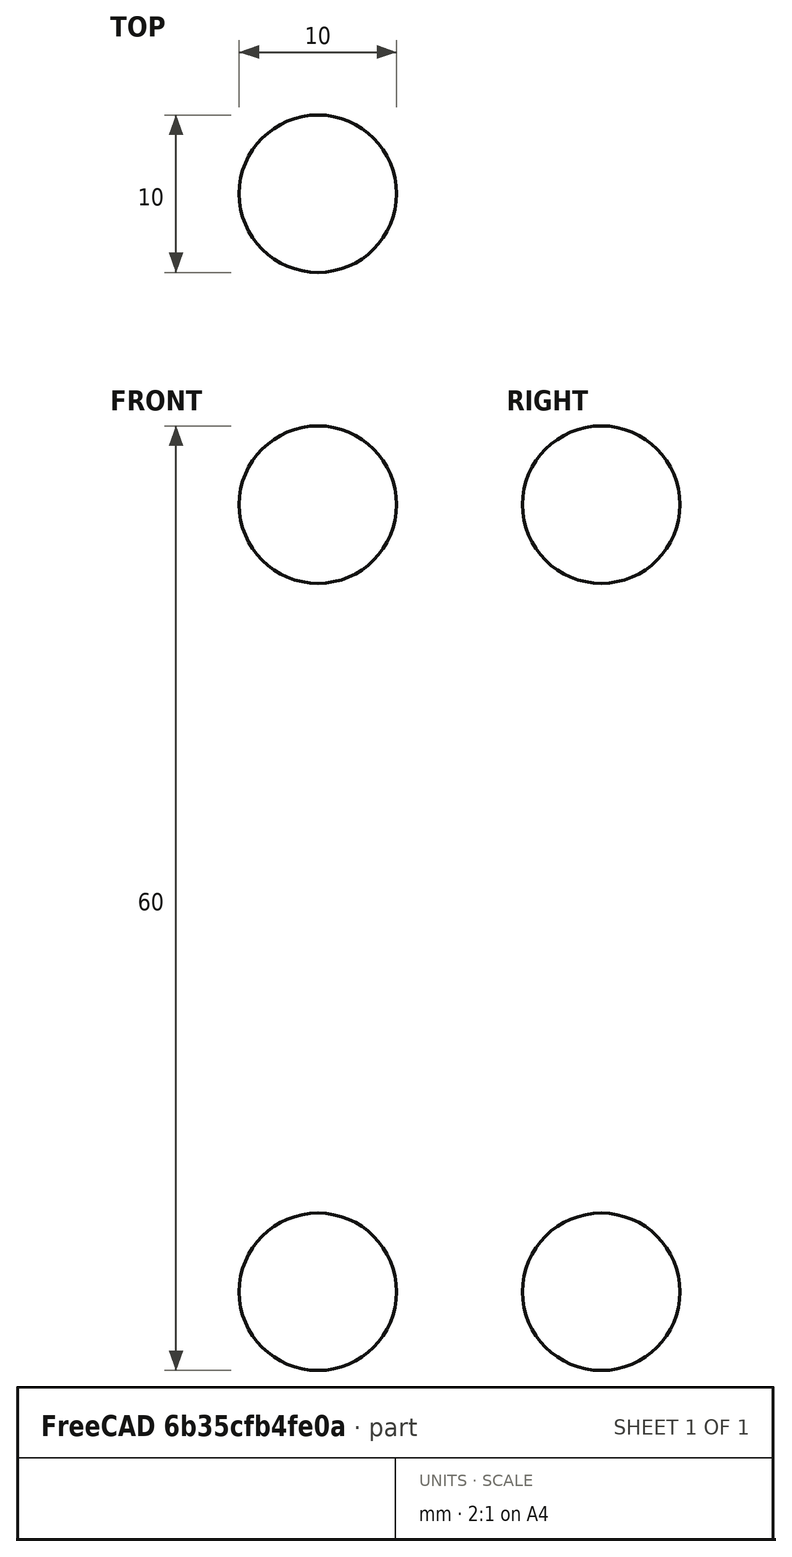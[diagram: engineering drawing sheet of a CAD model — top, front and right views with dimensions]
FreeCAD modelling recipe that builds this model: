
FCSTD DOCUMENT  (FreeCAD 0.22R35966 (Git))
Label: MassSpringDamper
License: All rights reserved
LicenseURL: http://en.wikipedia.org/wiki/All_rights_reserved
objects: App::DocumentObjectGroupPython×56, PartDesign::CoordinateSystem×6, App::TextDocument×3, Part::Line×3, App::Part×3, App::FeaturePython×2, Part::Sphere×2, Part::FeaturePython×2, App::DocumentObjectGroup×1, App::MaterialObjectPython×1
note: 13 computed .brp shape members not serialized (recipe doc carries the construction recipe); baked Part::Feature solids carry a one-line shape summary decoded from their .brp

FEATURE [App::DocumentObjectGroupPython] MBD_animated_vectors  # scripted group (container) (typed FeaturePython)
FEATURE [App::DocumentObjectGroupPython] MBD_constitutive_laws  # scripted group (container) (typed FeaturePython)
FEATURE [App::DocumentObjectGroupPython] MBD_drives_and_drive_callers  # scripted group (container) (typed FeaturePython)
FEATURE [App::DocumentObjectGroupPython] MBD_abstract_nodes  # scripted group (container) (typed FeaturePython)
FEATURE [App::DocumentObjectGroupPython] MBD_dummy_nodes  # scripted group (container) (typed FeaturePython)
FEATURE [App::DocumentObjectGroupPython] MBD_hydraulic_nodes  # scripted group (container) (typed FeaturePython)
FEATURE [App::DocumentObjectGroupPython] MBD_beam_elements  # scripted group (container) (typed FeaturePython)
FEATURE [App::DocumentObjectGroupPython] MBD_genel_clamps  # scripted group (container) (typed FeaturePython)
FEATURE [App::DocumentObjectGroupPython] MBD_genel_elements  # scripted group (container) (typed FeaturePython)
  Group = -> [MBD_genel_clamps]
FEATURE [App::DocumentObjectGroupPython] MBD_gravity_elements  # scripted group (container) (typed FeaturePython)
FEATURE [App::DocumentObjectGroupPython] MBD_hydraulic_fluid_elements  # scripted group (container) (typed FeaturePython)
FEATURE [App::DocumentObjectGroupPython] MBD_hydraulic_elements  # scripted group (container) (typed FeaturePython)
  Group = -> [MBD_hydraulic_fluid_elements]
FEATURE [App::DocumentObjectGroupPython] MBD_angular_acceleration_joints  # scripted group (container) (typed FeaturePython)
FEATURE [App::DocumentObjectGroupPython] MBD_angular_velocity_joints  # scripted group (container) (typed FeaturePython)
FEATURE [App::DocumentObjectGroupPython] MBD_assembly_joints  # scripted group (container) (typed FeaturePython)
FEATURE [App::DocumentObjectGroupPython] MBD_coincidence_joints  # scripted group (container) (typed FeaturePython)
FEATURE [App::DocumentObjectGroupPython] MBD_cylindrical_joints  # scripted group (container) (typed FeaturePython)
FEATURE [App::DocumentObjectGroupPython] MBD_deformable_axial_joints  # scripted group (container) (typed FeaturePython)
FEATURE [App::DocumentObjectGroupPython] MBD_deformable_displacement_joints  # scripted group (container) (typed FeaturePython)
FEATURE [App::DocumentObjectGroupPython] MBD_deformable_hinge_joints  # scripted group (container) (typed FeaturePython)
FEATURE [App::DocumentObjectGroupPython] MBD_distance_joints  # scripted group (container) (typed FeaturePython)
FEATURE [App::DocumentObjectGroupPython] MBD_drive_hinge_joints  # scripted group (container) (typed FeaturePython)
FEATURE [App::DocumentObjectGroupPython] MBD_in_line_joints  # scripted group (container) (typed FeaturePython)
FEATURE [App::DocumentObjectGroupPython] MBD_in_plane_joints  # scripted group (container) (typed FeaturePython)
FEATURE [App::DocumentObjectGroupPython] MBD_linear_acceleration_joints  # scripted group (container) (typed FeaturePython)
FEATURE [App::DocumentObjectGroupPython] MBD_linear_velocity_joints  # scripted group (container) (typed FeaturePython)
FEATURE [App::DocumentObjectGroupPython] MBD_prismatic_joints  # scripted group (container) (typed FeaturePython)
FEATURE [App::DocumentObjectGroupPython] MBD_hinge_joints  # scripted group (container) (typed FeaturePython)
FEATURE [App::DocumentObjectGroupPython] MBD_revolute_pin_joints  # scripted group (container) (typed FeaturePython)
FEATURE [App::DocumentObjectGroupPython] MBD_revolute_rotation_joints  # scripted group (container) (typed FeaturePython)
FEATURE [App::DocumentObjectGroupPython] MBD_shock_absorber_joints  # scripted group (container) (typed FeaturePython)
FEATURE [App::DocumentObjectGroupPython] MBD_slider_joints  # scripted group (container) (typed FeaturePython)
FEATURE [App::DocumentObjectGroupPython] MBD_spherical_hinge_joints  # scripted group (container) (typed FeaturePython)
FEATURE [App::DocumentObjectGroupPython] MBD_total_joints  # scripted group (container) (typed FeaturePython)
FEATURE [App::DocumentObjectGroupPython] MBD_total_pin_joints  # scripted group (container) (typed FeaturePython)
FEATURE [App::DocumentObjectGroupPython] MBD_viscous_body_joints  # scripted group (container) (typed FeaturePython)
FEATURE [App::DocumentObjectGroupPython] MBD_dummy_body_elements  # scripted group (container) (typed FeaturePython)
FEATURE [App::DocumentObjectGroupPython] MBD_gear_body_elements  # scripted group (container) (typed FeaturePython)
FEATURE [App::DocumentObjectGroupPython] MBD_structural_couple_elements  # scripted group (container) (typed FeaturePython)
FEATURE [App::DocumentObjectGroupPython] MBD_scalar_functions  # scripted group (container) (typed FeaturePython)
FEATURE [App::TextDocument] ELEMENT_input_file
  Text = <blob: 7349 chars omitted>
FEATURE [App::TextDocument] ELEMENT_input_file_aux
FEATURE [App::DocumentObjectGroupPython] MBD_input_files  # scripted group (container) (typed FeaturePython)
  Group = -> [ELEMENT_input_file,ELEMENT_input_file_aux]
FEATURE [App::TextDocument] ELEMENT_variables
  Text = K = 1; #Spring constant\nC = 0.01; #Damping constant
FEATURE [App::DocumentObjectGroupPython] MBD_user_defined_variables  # scripted group (container) (typed FeaturePython)
  Group = -> [ELEMENT_variables]
FEATURE [Part::Line] ELEMENT_cmx
  AttacherType = Attacher::AttachEngine3D
  X1 = -1e-16
  X2 = -1e-16
  Y1 = -1e-16
  Y2 = -1e-16
  Z1 = 2e-16
  Z2 = 50
FEATURE [Part::Line] ELEMENT_cmy
  AttacherType = Attacher::AttachEngine3D
  X1 = 0
  X2 = 0
  Y1 = 0
  Y2 = 0
  Z1 = 0
  Z2 = 1
FEATURE [Part::Line] ELEMENT_cmz
  AttacherType = Attacher::AttachEngine3D
  X1 = 0
  X2 = 0
  Y1 = 0
  Y2 = 0
  Z1 = 0
  Z2 = 1
FEATURE [PartDesign::CoordinateSystem] ELEMENT_ground
  AttacherType = Attacher::AttachEngine3D
FEATURE [App::DocumentObjectGroupPython] MBD_global_reference_frame  # scripted group (container) (typed FeaturePython)
  Group = -> [ELEMENT_cmx,ELEMENT_cmy,ELEMENT_cmz,ELEMENT_ground]
FEATURE [App::FeaturePython] ELEMENT_parameters  # WARN: FeaturePython — macro-defined, semantics opaque (R4)
  assembly_max_iterations = 1000
  default_orientation = 0
  derivatives_coefficient = auto
  derivatives_max_iterations = 100
  derivatives_tolerance = 0.0001
  final_time = 10
  initial_position_stiffness = 1
  initial_time = 0
  initial_velocity_stiffness = 1
  integration_max_iterations = 100
  model = 0
  modules_to_load = 0
  omega_rotates = 0
  output_data = 0
  output_meter = 1
  path_to_ELEMENT_executable = <userpath>/.local/share/FreeCAD/Mod/FreeCAD-motion-workbench-master/mbdyn-1.7.3-executables/LinuxExecutable/mbdyn
  print = 0
  skip_initial_joint_assembly = 0
  solver = 0
  time_step = 0.01
  tolerance = 1e-06
  type_of_path_to_ELEMENT_executable = 0
  type_of_path_to_run_time_loadable_modules = 0
  type_of_working_directory = 0
  units = 0
FEATURE [App::FeaturePython] ELEMENT_animation  # WARN: FeaturePython — macro-defined, semantics opaque (R4)
  animationClicked = false
  assembled = true
  association0 = none
  association1 = none
  association2 = none
  association3 = none
  association4 = none
  association5 = none
  association6 = none
  association7 = none
  association8 = none
  association9 = none
  bodies_line_width = 1
  bodies_point_size = 4
  characteristic_length = 100
  continous = true
  current_time = 0
  current_time_step = 0
  follow_selected_object = false
  highlight_element = true
  objects_to_animate = 0
  speed = 10
  stop_at_time = 0
  stop_at_time_step = 0
  subAssembly = true
  transparency_when_assembled = 0
  transparency_when_exploded = 50
  zoon_when_contracted = 0.5
  zoon_when_expanded = 1
FEATURE [App::DocumentObjectGroupPython] MBD_simulation_parameters  # scripted group (container) (typed FeaturePython)
  Group = -> [ELEMENT_parameters,ELEMENT_animation]
FEATURE [Part::Sphere] Sphere
  Angle1 = -90
  Angle2 = 90
  Angle3 = 360
  AttacherType = Attacher::AttachEngine3D
  Radius = 5
FEATURE [App::Part] Part  label="Grounded node"
  Group = -> [Sphere]
  Origin = -> Origin001
FEATURE [Part::Sphere] Sphere001
  Angle1 = -90
  Angle2 = 90
  Angle3 = 360
  AttacherType = Attacher::AttachEngine3D
  Radius = 5
FEATURE [App::Part] Part001  label="Oscillating mass"
  Group = -> [Sphere001]
  Origin = -> Origin002
  Placement = pos=(0,0,50) rot=(0,0,1;0rad)
FEATURE [App::DocumentObjectGroup] Group  label="CAD"
  Group = -> [Part,Part001]
FEATURE [Part::FeaturePython] ELEMENT_static_body_1  # WARN: FeaturePython — macro-defined, semantics opaque (R4)
  absolute_center_of_mass_X = 0
  absolute_center_of_mass_Y = -1e-16
  absolute_center_of_mass_Z = -1e-16
  base_entity = Part
  label = 1
  type = static
FEATURE [App::DocumentObjectGroupPython] MBD_static_body_elements  # scripted group (container) (typed FeaturePython)
  Group = -> [ELEMENT_static_body_1]
FEATURE [PartDesign::CoordinateSystem] ELEMENT_structural_static_1
  AttacherType = Attacher::AttachEngine3D
  Placement = pos=(0,-1e-16,-1e-16) rot=(0,0,1;0rad)
  absolute_angular_velocity_X = 0
  absolute_angular_velocity_Y = 0
  absolute_angular_velocity_Z = 0
  absolute_orientation_matrix = 3, 0.0, 0.0, 1.0, 2, 0.0, 1.0, 0.0
  absolute_position_X = 0
  absolute_position_Y = -1e-16
  absolute_position_Z = -1e-16
  absolute_velocity_X = 0
  absolute_velocity_Y = 0
  absolute_velocity_Z = 0
  base_entity = -> ELEMENT_static_body_1
  initial_conditions_reference_system_angular_velocity = 0
  initial_conditions_reference_system_velocity = 0
  label = 1
  offset_pitch = 0
  offset_reference_system_orientation = 0
  offset_reference_system_position = 0
  offset_roll = 0
  offset_x = 0
  offset_y = 0
  offset_yaw = 0
  offset_z = 0
  placement_method = 0
  plugin_variables = none
  type = static
FEATURE [App::DocumentObjectGroupPython] MBD_structural_static_nodes  # scripted group (container) (typed FeaturePython)
  Group = -> [ELEMENT_structural_static_1]
FEATURE [PartDesign::CoordinateSystem] ELEMENT_clamp_joint_1
  AttacherType = Attacher::AttachEngine3D
  Placement = pos=(0,-1e-16,-1e-16) rot=(0,0,1;0rad)
  absolute_orientation_matrix = 3, 0.0, 0.0, 1.0, 2, 0.0, 1.0, 0.0
  absolute_pin_position_X = 0
  absolute_pin_position_Y = -1e-16
  absolute_pin_position_Z = -1e-16
  assembly_joint = false
  base_entity = -> ELEMENT_static_body_1
  driven_element = false
  driven_element_expression = Time <= 1.0
  group = 0
  joint = clamp
  joint_activation = 0
  label = 1
  plugin_variables = none
FEATURE [App::DocumentObjectGroupPython] MBD_clamp_joints  # scripted group (container) (typed FeaturePython)
  Group = -> [ELEMENT_clamp_joint_1]
FEATURE [App::DocumentObjectGroupPython] MBD_joint_elements  # scripted group (container) (typed FeaturePython)
  Group = -> [MBD_angular_acceleration_joints,MBD_angular_velocity_joints,MBD_assembly_joints,MBD_clamp_joints,MBD_coincidence_joints,MBD_cylindrical_joints,MBD_deformable_axial_joints,MBD_deformable_displacement_joints,MBD_deformable_hinge_joints,MBD_distance_joints,MBD_drive_hinge_joints,MBD_in_line_joints,MBD_in_plane_joints,MBD_linear_acceleration_joints,MBD_linear_velocity_joints,MBD_prismatic_joints,+9 more]
FEATURE [Part::FeaturePython] ELEMENT_rigid_body_2  # WARN: FeaturePython — macro-defined, semantics opaque (R4)
  FirstAxisOfInertia = (0,0,1)
  Ixx = 0.0413643
  Iyy = 0.0413643
  Izz = 0.0413643
  SecondAxisOfInertia = (0,-1,0)
  ThirdAxisOfInertia = (1,0,0)
  absolute_center_of_mass_X = 0
  absolute_center_of_mass_Y = -1e-16
  absolute_center_of_mass_Z = 50
  base_entity = Part001
  density = 7.9e-06
  ixx = 5235.99
  iyy = 5235.99
  izz = 5235.99
  label = 2
  mass = 0.00413643
  material = Steel-Generic
  material_definition = 0
  material_object = ELEMENT_material_2
  node = 2
  relative_center_of_mass_X = 0
  relative_center_of_mass_Y = 0
  relative_center_of_mass_Z = 0
  type = rigid
  volume = 523.599
FEATURE [App::DocumentObjectGroupPython] MBD_rigid_body_elements  # scripted group (container) (typed FeaturePython)
  Group = -> [ELEMENT_rigid_body_2]
FEATURE [App::Part] MBD_body_elements
  Group = -> [MBD_dummy_body_elements,MBD_rigid_body_elements,MBD_gear_body_elements,MBD_static_body_elements,ELEMENT_static_body_1,ELEMENT_rigid_body_2]
  Origin = -> Origin
FEATURE [App::MaterialObjectPython] ELEMENT_material_2  # material (typed FeaturePython)
  Category = 0
  Material = Density=7900.00 kg/m^3; Name=Steel-Generic
FEATURE [App::DocumentObjectGroupPython] MBD_materials  # scripted group (container) (typed FeaturePython)
  Group = -> [ELEMENT_material_2]
FEATURE [PartDesign::CoordinateSystem] ELEMENT_structural_dynamic_2
  AttacherType = Attacher::AttachEngine3D
  Placement = pos=(0,-1e-16,50) rot=(0,0,1;0rad)
  absolute_angular_velocity_X = 0
  absolute_angular_velocity_Y = 0
  absolute_angular_velocity_Z = 0
  absolute_orientation_matrix = 3, 0.0, 0.0, 1.0, 2, 0.0, 1.0, 0.0
  absolute_position_X = 0
  absolute_position_Y = -1e-16
  absolute_position_Z = 50
  absolute_velocity_X = 0
  absolute_velocity_Y = 0
  absolute_velocity_Z = 300
  base_entity = -> ELEMENT_rigid_body_2
  initial_conditions_reference_system_angular_velocity = 0
  initial_conditions_reference_system_velocity = 0
  label = 2
  offset_pitch = 0
  offset_reference_system_orientation = 0
  offset_reference_system_position = 0
  offset_roll = 0
  offset_x = 0
  offset_y = 0
  offset_yaw = 0
  offset_z = 0
  placement_method = 0
  plugin_variables = "X_3_2": position in global direction 3 \n"x_3_2": position in direction 3, in the reference frame of the node \n"XP_3_2": velocity in global direction 3 \n"xP_3_2": velocity in direction 3, in the reference frame of the node
  type = dynamic
FEATURE [App::DocumentObjectGroupPython] MBD_structural_dynamic_nodes  # scripted group (container) (typed FeaturePython)
  Group = -> [ELEMENT_structural_dynamic_2]
FEATURE [App::DocumentObjectGroupPython] MBD_nodes  # scripted group (container) (typed FeaturePython)
  Group = -> [MBD_abstract_nodes,MBD_dummy_nodes,MBD_structural_dynamic_nodes,MBD_hydraulic_nodes,MBD_structural_static_nodes]
FEATURE [PartDesign::CoordinateSystem] ELEMENT_marker_2_1
  AttacherType = Attacher::AttachEngine3D
  Placement = pos=(-1e-16,-1e-16,50) rot=(0,0,1;0rad)
  base_entity = -> ELEMENT_rigid_body_2
  label = 2
  offset_pitch = 0
  offset_reference_system_orientation = 0
  offset_reference_system_position = 0
  offset_roll = 0
  offset_x = 0
  offset_y = 0
  offset_yaw = 0
  offset_z = 0
  placement_method = 1
  position_reference_1 = -> ELEMENT_rigid_body_2 [Face1]
FEATURE [App::DocumentObjectGroupPython] MBD_markers  # scripted group (container) (typed FeaturePython)
  Group = -> [ELEMENT_marker_2_1]
FEATURE [PartDesign::CoordinateSystem] ELEMENT_structural_internal_force_1
  AttacherType = Attacher::AttachEngine3D
  Placement = pos=(-1e-16,-1e-16,2e-16) rot=(0,0,1;0rad)
  action_entity = -> ELEMENT_marker_2_1
  base_entity = -> ELEMENT_static_body_1
  contact_damping_activation_depth = 1e-06
  contact_damping_coefficient = 10
  contact_direction = 0
  contact_model = 0
  contact_offset = 0
  contact_stiffness_coefficient = 1000000
  contact_stiffness_exponent = 1.2
  contact_type = 0
  direction = 0.0, 0.0, 1.0
  driven_element_expression = Time <= 1.0
  element_activation = 0
  force = structural internal force
  force_value = K * (X_3_2 - Pz_2) + C * XP_3_2
  label = 1
  offset_pitch = 0
  offset_reference_system_orientation = 0
  offset_reference_system_position = 0
  offset_roll = 0
  offset_x = 0
  offset_y = 0
  offset_yaw = 0
  offset_z = 0
  placement_method = 1
  position_reference_1 = -> ELEMENT_static_body_1 [Face1]
  relative_arm_1 = -4.576362771356912e-20, -9.10421811376138e-20, 2.4513724383723465e-19
  relative_arm_2 = -9.746037860749074e-20, -4.813322392031539e-20, 0.0
  type = 1
FEATURE [App::DocumentObjectGroupPython] MBD_structural_force_elements  # scripted group (container) (typed FeaturePython)
  Group = -> [ELEMENT_structural_internal_force_1]
FEATURE [App::DocumentObjectGroupPython] MBD_elements  # scripted group (container) (typed FeaturePython)
  Group = -> [MBD_beam_elements,MBD_body_elements,MBD_genel_elements,MBD_gravity_elements,MBD_hydraulic_elements,MBD_joint_elements,MBD_structural_couple_elements,MBD_structural_force_elements]
FEATURE [App::DocumentObjectGroupPython] MBD_simulation  # scripted group (container) (typed FeaturePython)
  Group = -> [MBD_animated_vectors,MBD_constitutive_laws,MBD_drives_and_drive_callers,MBD_global_reference_frame,MBD_input_files,MBD_materials,MBD_markers,MBD_nodes,MBD_elements,MBD_simulation_parameters,MBD_scalar_functions,MBD_user_defined_variables]
